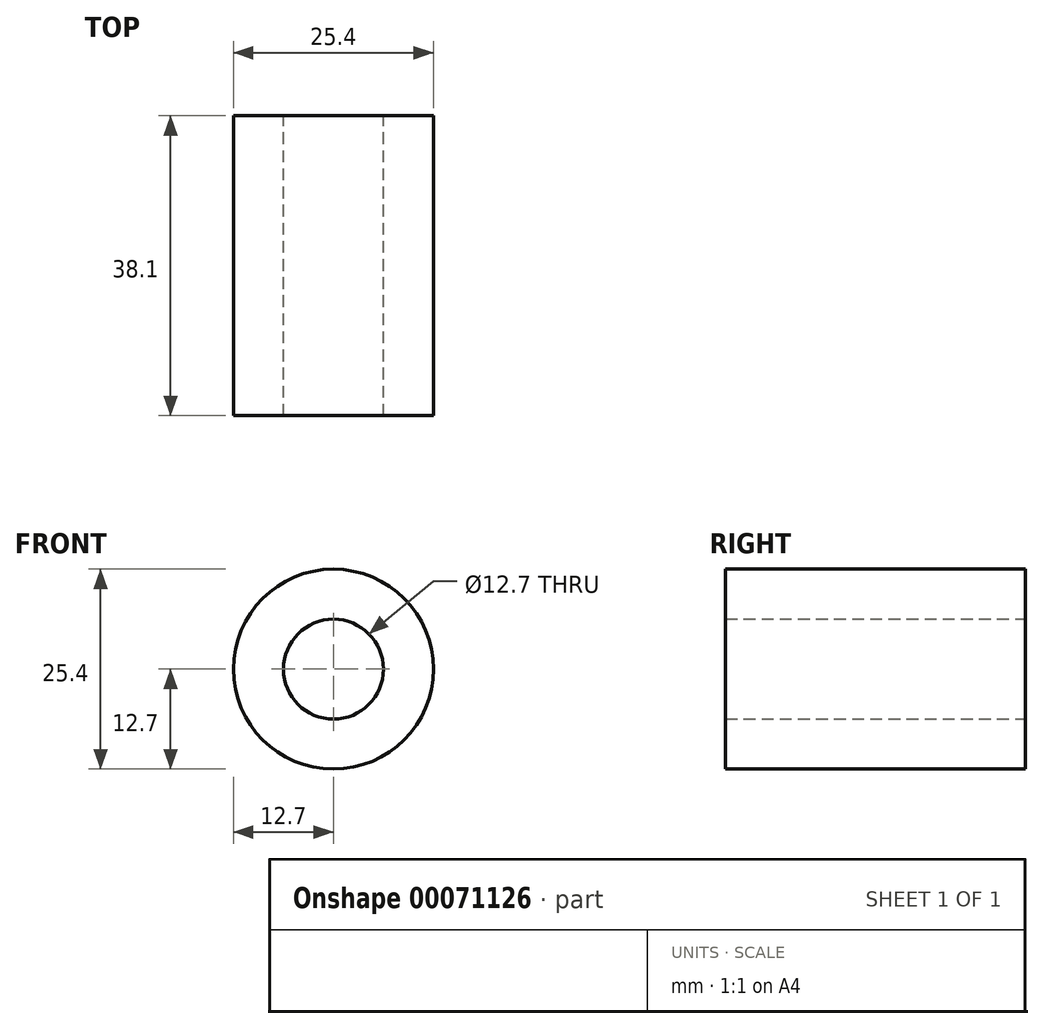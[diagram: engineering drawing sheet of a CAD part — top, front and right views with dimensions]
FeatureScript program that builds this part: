
annotation { "Feature Type Name" : "Feature", "Feature Type Description" : "" }
export const myFeature = defineFeature(function(context is Context, id is Id, definition is map)
    precondition{}
    {
        {
            var Q0;
            Q0=qCreatedBy(makeId("Front.planeOp"),FACE);
            var sketch = newSketch(context, id + "F0", { "sketchPlane" : qUnion([Q0])});
            skCircle(sketch, "E0", {"center": v(0, 0) * mm, "radius": 12.7 * mm});
            skCircle(sketch, "E1", {"center": v(0, 0) * mm, "radius": 6.35 * mm});
            skSolve(sketch);
        }
        {
            var Q0;
            Q0 = qSketchRegion(id + "F0", true);
            extrude(context, id + "F1", {"entities" : qUnion([Q0]), "depth" : 38.1 * mm});
        }
    });
